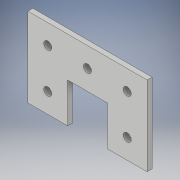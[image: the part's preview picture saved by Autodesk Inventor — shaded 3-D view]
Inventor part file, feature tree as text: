
AUTODESK INVENTOR PART (.ipt)
format: ipt  version: 2018 (Build 220112000, 112)  size: 113,664 bytes
history: native  units: in
note: dims shown in document units (in); Inventor stores cm internally (conversion verified against a paired STEP export)
features: extrude x1, sketch x1
ambient origin geometry x8: Origin, YZ Plane, XZ Plane, XY Plane, X Axis, Y Axis, Z Axis, Center Point
bodies: Body1 (feature_tree)
feature tree (2):
  extrude  "Extrusion2"  Depth=2.0in
  sketch  "Sketch1"  dims[d0=1.0in d1=2.0in d5=0.5in d6=1.0in d7=1.0in d11=0.2031in d14=1.0in d15=1.0in d16=1.0in d17=1.0in d18=0.125in d19=0.0in]
